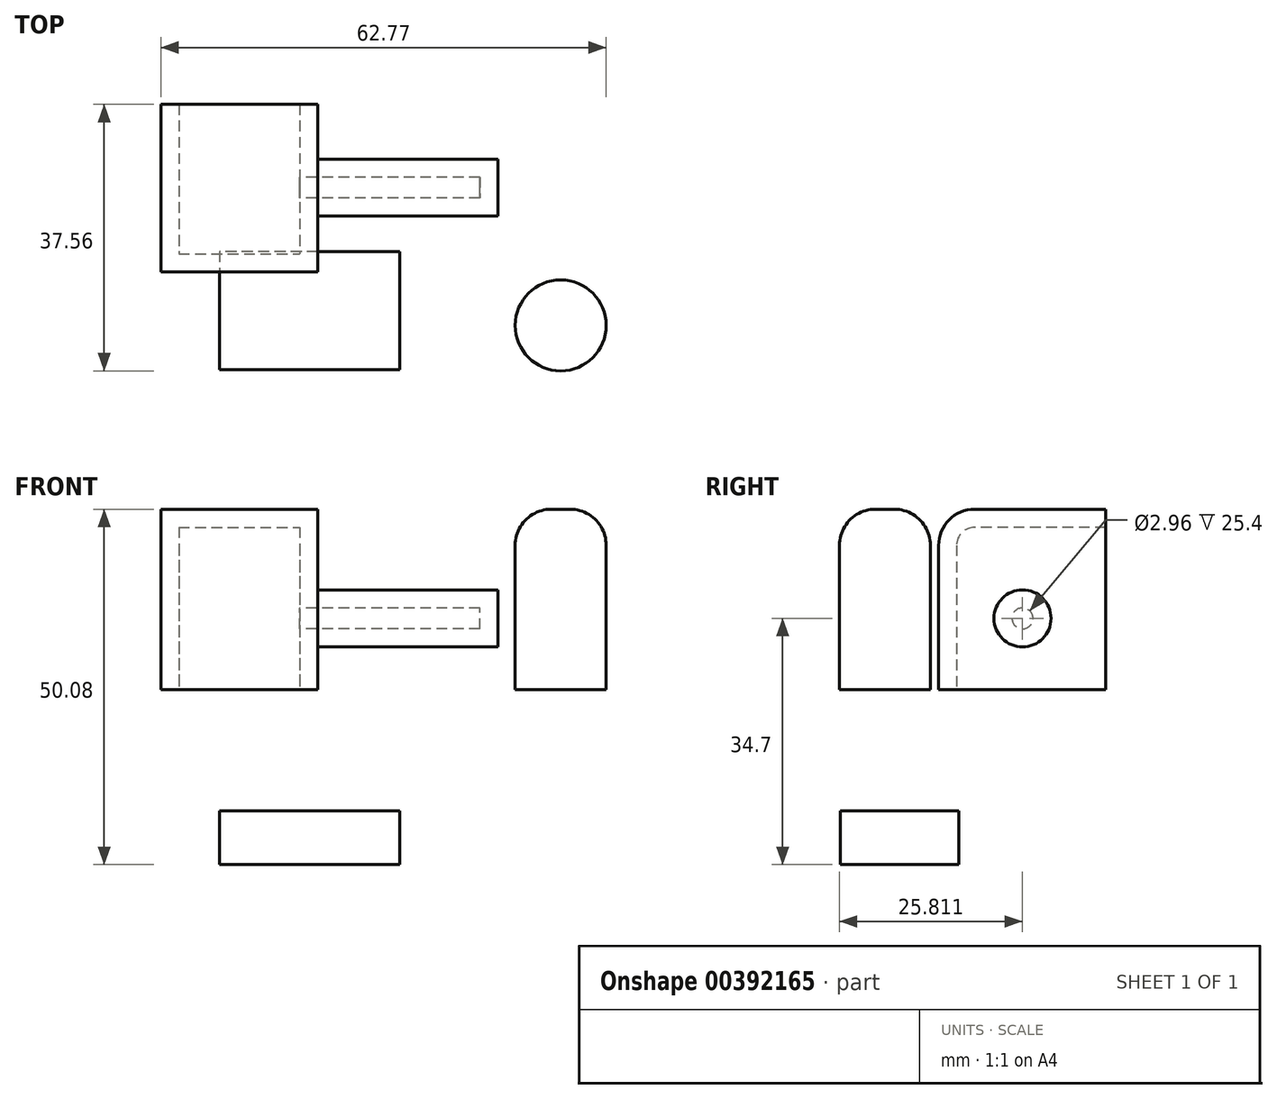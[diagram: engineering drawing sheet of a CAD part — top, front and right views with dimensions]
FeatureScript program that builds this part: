
annotation { "Feature Type Name" : "Feature", "Feature Type Description" : "" }
export const myFeature = defineFeature(function(context is Context, id is Id, definition is map)
    precondition{}
    {
        {
            var Q0;
            Q0=qCreatedBy(makeId("Top.planeOp"),FACE);
            var sketch = newSketch(context, id + "F0", { "sketchPlane" : qUnion([Q0])});
            skLineSegment(sketch, "E0.bottom", {"start": v(17.49, -18.63) * mm, "end": v(19.01, -18.63) * mm});
            skLineSegment(sketch, "E0.top", {"start": v(17.49, -22.53) * mm, "end": v(19.01, -22.53) * mm});
            skLineSegment(sketch, "E0.left", {"start": v(17.49, -18.63) * mm, "end": v(17.49, -22.53) * mm});
            skLineSegment(sketch, "E0.right", {"start": v(19.01, -18.63) * mm, "end": v(19.01, -22.53) * mm});
            skLineSegment(sketch, "E1.bottom", {"start": v(-8.29, 6.47) * mm, "end": v(13.82, 6.47) * mm});
            skLineSegment(sketch, "E1.top", {"start": v(-8.29, -17.11) * mm, "end": v(13.82, -17.11) * mm});
            skLineSegment(sketch, "E1.left", {"start": v(-8.29, 6.47) * mm, "end": v(-8.29, -17.11) * mm});
            skLineSegment(sketch, "E1.right", {"start": v(13.82, 6.47) * mm, "end": v(13.82, -17.11) * mm});
            skSolve(sketch);
        }
        {
            var Q0;
            Q0=makeQuery(id+"F0.imprint","IMPRINT",FACE,{"disambiguationData":[TD([[makeQuery(id+"F0.imprint","IMPRINT",EDGE,{"derivedFrom":sQuery(id+"F0.wireOp",EDGE,"E1.bottom")}),-1.0]])]});
            extrude(context, id + "F1", {"entities" : qUnion([Q0]), "depth" : 25.4 * mm});
        }
        {
            var Q0;
            Q0=makeQuery(id+"F1.opExtrude","SWEPT_FACE",FACE,{"disambiguationData":[OSD([sQuery(id+"F0.wireOp",EDGE,"E1.right")])]});
            var sketch = newSketch(context, id + "F2", { "sketchPlane" : qUnion([Q0])});
            skSolve(sketch);
        }
        {
            var Q0;
            Q0=qCreatedBy(makeId("Top.planeOp"),FACE);
            var sketch = newSketch(context, id + "F3", { "sketchPlane" : qUnion([Q0])});
            skCircle(sketch, "E2", {"center": v(48.07, -24.68) * mm, "radius": 6.4 * mm});
            skSolve(sketch);
        }
        {
            var Q0;
            Q0 = qSketchRegion(id + "F3", true);
            extrude(context, id + "F4", {"entities" : qUnion([Q0]), "depth" : 25.4 * mm});
        }
        {
            var Q0;
            Q0=makeQuery(id+"F1.opExtrude","CAP_EDGE",EDGE,{"disambiguationData":[OSD([sQuery(id+"F0.wireOp",EDGE,"E1.top")])],"isStart":false});
            var Q1;
            Q1=makeQuery(id+"F4.opExtrude","CAP_FACE",FACE,{"disambiguationData":[OSD([sQuery(id+"F3.wireOp",EDGE,"E2")])],"isStart":false});
            var Q2;
            Q2=makeQuery(id+"F4.opExtrude","CAP_EDGE",EDGE,{"disambiguationData":[OSD([sQuery(id+"F3.wireOp",EDGE,"E2")])],"isStart":false});
            fillet(context, id + "F5", {"entities" : qUnion([Q0, Q1, Q2]), "radius" : 5.08 * mm, "tangentPropagation" : true, "allowEdgeOverflow" : false});
        }
        {
            var Q0;
            {var subQ0=sQuery(id+"F0.wireOp",EDGE,"E1.right");Q0=makeQuery(id+"F2.imprint","IMPRINT",FACE,{"disambiguationData":[TD([[makeQuery(id+"F2.imprint","IMPRINT",EDGE,{"derivedFrom":makeQuery(id+"F1.opExtrude","CAP_EDGE",EDGE,{"disambiguationData":[OSD([subQ0])],"isStart":true})}),-1.0]])]});}
            var sketch = newSketch(context, id + "F6", { "sketchPlane" : qUnion([Q0])});
            skCircle(sketch, "E3", {"center": v(-5.28, 10.02) * mm, "radius": 4.02 * mm});
            skPoint(sketch, "E3.first.point", {"position": v(-1.5, 8.67) * mm});
            skPoint(sketch, "E3.second.point", {"position": v(-1.94, 7.78) * mm});
            skPoint(sketch, "E3.third.point", {"position": v(-9.1, 11.26) * mm});
            skSolve(sketch);
        }
        {
            var Q0;
            Q0 = qSketchRegion(id + "F6", true);
            extrude(context, id + "F7", {"entities" : qUnion([Q0]), "operationType" : NewBodyOperationType.ADD, "depth" : 25.4 * mm});
        }
        {
            var Q0;
            Q0=makeQuery(id+"F1.opExtrude","CAP_FACE",FACE,{"disambiguationData":[OSD([sQuery(id+"F0.wireOp",EDGE,"E1.bottom"),sQuery(id+"F0.wireOp",EDGE,"E1.top"),sQuery(id+"F0.wireOp",EDGE,"E1.left"),sQuery(id+"F0.wireOp",EDGE,"E1.right")])],"isStart":true});
            var Q1;
            Q1=makeQuery(id+"F1.opExtrude","SWEPT_FACE",FACE,{"disambiguationData":[OSD([sQuery(id+"F0.wireOp",EDGE,"E1.bottom")])]});
            shell(context, id + "F8", {"entities" : qUnion([Q0, Q1]), "thickness" : 2.54 * mm});
        }
        {
            var Q0;
            Q0=qCreatedBy(makeId("Right.planeOp"),FACE);
            var sketch = newSketch(context, id + "F9", { "sketchPlane" : qUnion([Q0])});
            skLineSegment(sketch, "E4.bottom", {"start": v(-14.28, -17.1) * mm, "end": v(-30.94, -17.1) * mm});
            skLineSegment(sketch, "E4.top", {"start": v(-14.28, -24.68) * mm, "end": v(-30.94, -24.68) * mm});
            skLineSegment(sketch, "E4.left", {"start": v(-14.28, -17.1) * mm, "end": v(-14.28, -24.68) * mm});
            skLineSegment(sketch, "E4.right", {"start": v(-30.94, -17.1) * mm, "end": v(-30.94, -24.68) * mm});
            skPoint(sketch, "E4.middle", {"position": v(-22.6, -20.89) * mm});
            skSolve(sketch);
        }
        {
            var Q0;
            Q0=makeQuery(id+"F9.imprint","IMPRINT",FACE,{"disambiguationData":[TD([[makeQuery(id+"F9.imprint","IMPRINT",EDGE,{"derivedFrom":sQuery(id+"F9.wireOp",EDGE,"E4.bottom")}),1.0]])]});
            extrude(context, id + "F10", {"entities" : qUnion([Q0]), "depth" : 25.4 * mm});
        }
    });
